# Revit family: Windows_Direct-Set-Wide_CityLine_Quaker-Windows
name_source: partatom
category: Windows
units: mm (PartAtom-declared; Revit-internal decimal feet)

## family parameters
Always vertical = Yes
Classification Number = 23.30.20.00
Cut with Voids When Loaded = No
Host = Wall
Room Calculation Point = No
Shared = No

## types (2) — shared parameters
Analytic Construction = <None>
Default Sill Height = 36"
Define Thermal Properties by = Schematic Type
Frame Material = Architectural Grade 6063-T63 Aluminum
Glass Material = Glass, Clear Glazing, Tempered
Height = 99"
Keynote = 08 51 13
Manufacturer = Quaker Windows & Doors
Model = C605 Direct Set Wide
Product Page URL = https://www.arcat.com
Rough Height = 99 1/4"
Rough Width = 60 1/4"
URL = https://www.quartzluxurywindows.com
Wall Closure = By host
Width = 60"

## per-type parameters (varying)
| type | Bevel Exterior | Description | Squared Off Exterior |
| 60" x 99", Squared Off Exterior | No | Direct Set Wide Window, Single, Squared Off Exterior | Yes |
| 60" x 99", Bevel Exterior | Yes | Direct Set Wide Window, Single, Bevel Exterior | No |

## geometry (parser evidence)
native form markers: Sweep x9
no freeform markers — native parametric forms only
